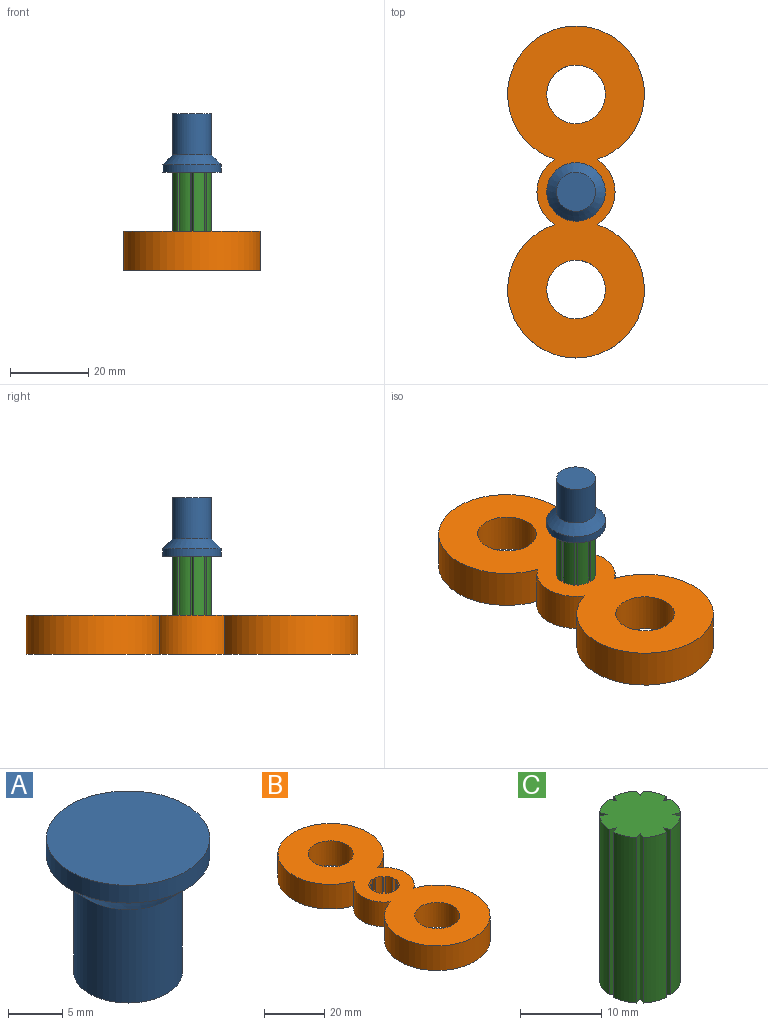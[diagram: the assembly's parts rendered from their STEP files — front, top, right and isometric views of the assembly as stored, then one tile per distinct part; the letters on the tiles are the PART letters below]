
ASSEMBLY  parts=3 mates=2
PART A: 5 faces, bbox 15x15x15 mm
  f0: cylinder r=5mm len=10.5mm, axis (0,0,-1), area 329.9mm2, adj f1,f4
  f1: plane 10x10mm, normal (0,0,-1), area 78.5mm2, adj f0
  f2: cylinder r=7.5mm len=15mm, axis (0,0,-1), area 94.2mm2, adj f3,f4
  f3: plane 15x15mm, normal (0,0,1), area 176.7mm2, adj f2
  f4: cone r=7.5mm half-angle=45deg, axis (0,0,1), area 138.8mm2, adj f0,f2
PART B: 32 faces, bbox 35x85x10 mm
  f0: cylinder r=5mm len=10mm, axis (0,0,-1), area 31.6mm2, adj f14,f15,f21,f30
  f1: cylinder r=5mm len=10mm, axis (0,0,-1), area 31.6mm2, adj f14,f15,f23,f28
  f2: cylinder r=5mm len=10mm, axis (0,0,-1), area 31.6mm2, adj f14,f15,f19,f26
  f3: cylinder r=5mm len=10mm, axis (0,0,-1), area 31.6mm2, adj f14,f15,f17,f24
  f4: cylinder r=5mm len=10mm, axis (0,0,-1), area 31.6mm2, adj f14,f15,f22,f25
  f5: cylinder r=5mm len=10mm, axis (0,0,-1), area 31.6mm2, adj f14,f15,f20,f27
  f6: cylinder r=5mm len=10mm, axis (0,0,-1), area 31.6mm2, adj f14,f15,f18,f29
  f7: cylinder r=17.5mm len=35mm, axis (0,0,-1), area 988.4mm2, adj f8,f11,f14,f15
  f8: cylinder r=10mm len=16.75mm, axis (0,0,-1), area 198.5mm2, adj f7,f9,f14,f15
  f9: cylinder r=17.5mm len=35mm, axis (0,0,-1), area 988.4mm2, adj f8,f11,f14,f15
  f10: cylinder r=5mm len=10mm, axis (0,0,-1), area 31.6mm2, adj f14,f15,f16,f31
  f11: cylinder r=10mm len=16.75mm, axis (0,0,-1), area 198.5mm2, adj f7,f9,f14,f15
  f12: cylinder r=7.5mm len=15mm, axis (0,0,-1), area 471.2mm2, adj f14,f15
  f13: cylinder r=7.5mm len=15mm, axis (0,0,-1), area 471.2mm2, adj f14,f15
  f14: plane 85x35mm, normal (0,0,1), area 1772.4mm2, adj f0,f1,f2,f3,f4,f5,f6,f7
  f15: plane 85x35mm, normal (0,0,-1), area 1772.4mm2, adj f0,f1,f2,f3,f4,f5,f6,f7
  f16: plane 10x0.92mm, normal (0.38,-0.92,0), area 10mm2, adj f10,f14,f15,f17
  f17: plane 10x0.92mm, normal (0.38,0.92,0), area 10mm2, adj f3,f14,f15,f16
  f18: plane 10x0.92mm, normal (-0.38,0.92,0), area 10mm2, adj f6,f14,f15,f19
  f19: plane 10x0.92mm, normal (-0.38,-0.92,0), area 10mm2, adj f2,f14,f15,f18
  f20: plane 10x0.92mm, normal (0.92,0.38,0), area 10mm2, adj f5,f14,f15,f21
  f21: plane 10x0.92mm, normal (-0.92,0.38,0), area 10mm2, adj f0,f14,f15,f20
  f22: plane 10x0.92mm, normal (-0.92,-0.38,0), area 10mm2, adj f4,f14,f15,f23
  f23: plane 10x0.92mm, normal (0.92,-0.38,0), area 10mm2, adj f1,f14,f15,f22
  f24: plane 10x0.92mm, normal (-0.38,-0.92,0), area 10mm2, adj f3,f14,f15,f25
  f25: plane 10x0.92mm, normal (0.92,0.38,0), area 10mm2, adj f4,f14,f15,f24
  f26: plane 10x0.92mm, normal (0.38,0.92,0), area 10mm2, adj f2,f14,f15,f27
  f27: plane 10x0.92mm, normal (-0.92,-0.38,0), area 10mm2, adj f5,f14,f15,f26
  f28: plane 10x0.92mm, normal (-0.92,0.38,0), area 10mm2, adj f1,f14,f15,f29
  f29: plane 10x0.92mm, normal (0.38,-0.92,0), area 10mm2, adj f6,f14,f15,f28
  f30: plane 10x0.92mm, normal (0.92,-0.38,0), area 10mm2, adj f0,f14,f15,f31
  f31: plane 10x0.92mm, normal (-0.38,0.92,0), area 10mm2, adj f10,f14,f15,f30
PART C: 26 faces, bbox 10x10x25 mm
  f0: plane 25x0.92mm, normal (-0.92,-0.38,0), area 25mm2, adj f1,f23,f24,f25
  f1: plane 25x0.92mm, normal (0.38,0.92,0), area 25mm2, adj f0,f2,f24,f25
  f2: cylinder r=5mm len=25mm, axis (0,0,-1), area 79mm2, adj f1,f3,f24,f25
  f3: plane 25x0.92mm, normal (-0.38,-0.92,0), area 25mm2, adj f2,f4,f24,f25
  f4: plane 25x0.92mm, normal (-0.38,0.92,0), area 25mm2, adj f3,f5,f24,f25
  f5: cylinder r=5mm len=25mm, axis (0,0,-1), area 79mm2, adj f4,f6,f24,f25
  f6: plane 25x0.92mm, normal (0.38,-0.92,0), area 25mm2, adj f5,f7,f24,f25
  f7: plane 25x0.92mm, normal (-0.92,0.38,0), area 25mm2, adj f6,f8,f24,f25
  f8: cylinder r=5mm len=25mm, axis (0,0,-1), area 79mm2, adj f7,f9,f24,f25
  f9: plane 25x0.92mm, normal (0.92,-0.38,0), area 25mm2, adj f8,f10,f24,f25
  f10: plane 25x0.92mm, normal (-0.92,-0.38,0), area 25mm2, adj f9,f11,f24,f25
  f11: cylinder r=5mm len=25mm, axis (0,0,-1), area 79mm2, adj f10,f12,f24,f25
  f12: plane 25x0.92mm, normal (0.92,0.38,0), area 25mm2, adj f11,f13,f24,f25
  f13: plane 25x0.92mm, normal (-0.38,-0.92,0), area 25mm2, adj f12,f14,f24,f25
  f14: cylinder r=5mm len=25mm, axis (0,0,-1), area 79mm2, adj f13,f15,f24,f25
  f15: plane 25x0.92mm, normal (0.38,0.92,0), area 25mm2, adj f14,f16,f24,f25
  f16: plane 25x0.92mm, normal (0.38,-0.92,0), area 25mm2, adj f15,f17,f24,f25
  f17: cylinder r=5mm len=25mm, axis (0,0,-1), area 79mm2, adj f16,f18,f24,f25
  f18: plane 25x0.92mm, normal (-0.38,0.92,0), area 25mm2, adj f17,f19,f24,f25
  f19: plane 25x0.92mm, normal (0.92,-0.38,0), area 25mm2, adj f18,f20,f24,f25
  f20: cylinder r=5mm len=25mm, axis (0,0,-1), area 79mm2, adj f19,f21,f24,f25
  f21: plane 25x0.92mm, normal (-0.92,0.38,0), area 25mm2, adj f20,f22,f24,f25
  f22: plane 25x0.92mm, normal (0.92,0.38,0), area 25mm2, adj f21,f23,f24,f25
  f23: cylinder r=5mm len=25mm, axis (0,0,-1), area 79mm2, adj f0,f22,f24,f25
  f24: plane 9.97x9.97mm, normal (0,0,1), area 75.7mm2, adj f0,f1,f2,f3,f4,f5,f6,f7
  f25: plane 9.97x9.97mm, normal (0,0,-1), area 75.7mm2, adj f0,f1,f2,f3,f4,f5,f6,f7
PLACE A rot(axis=(1,0,0),180deg) t=(-2.73,-0.53,36.56)mm
PLACE B t=(-2.73,-0.53,-3.44)mm
PLACE C rot(axis=(1,0,0),180deg) t=(-2.73,-0.53,21.56)mm
MATE fastened C.f5 <-> B.f11  axis (0,0,-1) through (-2.73,-0.53,-3.44)mm
MATE fastened A.f2 <-> C.f2  axis (0,0,-1) through (-2.73,-0.53,21.56)mm
